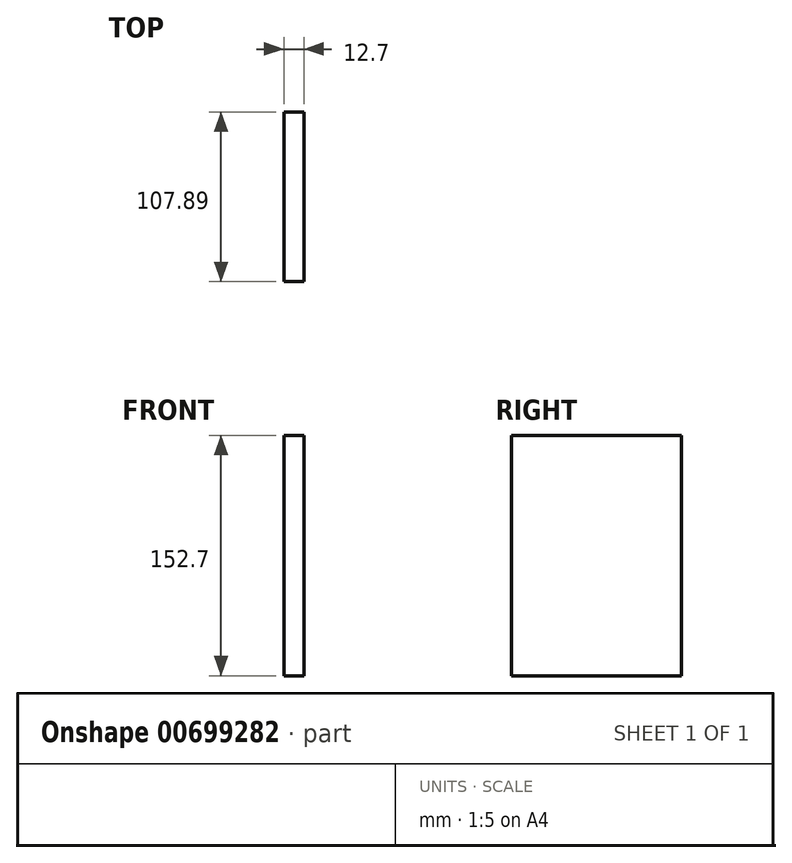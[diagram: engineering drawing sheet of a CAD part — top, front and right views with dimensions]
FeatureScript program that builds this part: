
annotation { "Feature Type Name" : "Feature", "Feature Type Description" : "" }
export const myFeature = defineFeature(function(context is Context, id is Id, definition is map)
    precondition{}
    {
        {
            var Q0;
            Q0=qCreatedBy(makeId("Right.planeOp"),FACE);
            var sketch = newSketch(context, id + "F0", { "sketchPlane" : qUnion([Q0])});
            skLineSegment(sketch, "E0.bottom", {"start": v(52.98, 76.5) * mm, "end": v(-54.91, 76.5) * mm});
            skLineSegment(sketch, "E0.top", {"start": v(52.98, -76.2) * mm, "end": v(-54.91, -76.2) * mm});
            skLineSegment(sketch, "E0.left", {"start": v(52.98, 76.5) * mm, "end": v(52.98, -76.2) * mm});
            skLineSegment(sketch, "E0.right", {"start": v(-54.91, 76.5) * mm, "end": v(-54.91, -76.2) * mm});
            skSolve(sketch);
        }
        {
            var Q0;
            Q0=makeQuery(id+"F0.imprint","IMPRINT",FACE,{"disambiguationData":[TD([[makeQuery(id+"F0.imprint","IMPRINT",EDGE,{"derivedFrom":sQuery(id+"F0.wireOp",EDGE,"E0.bottom")}),1.0]])]});
            extrude(context, id + "F1", {"entities" : qUnion([Q0]), "depth" : 12.7 * mm, "offsetDistance" : 25.4 * mm});
        }
    });
